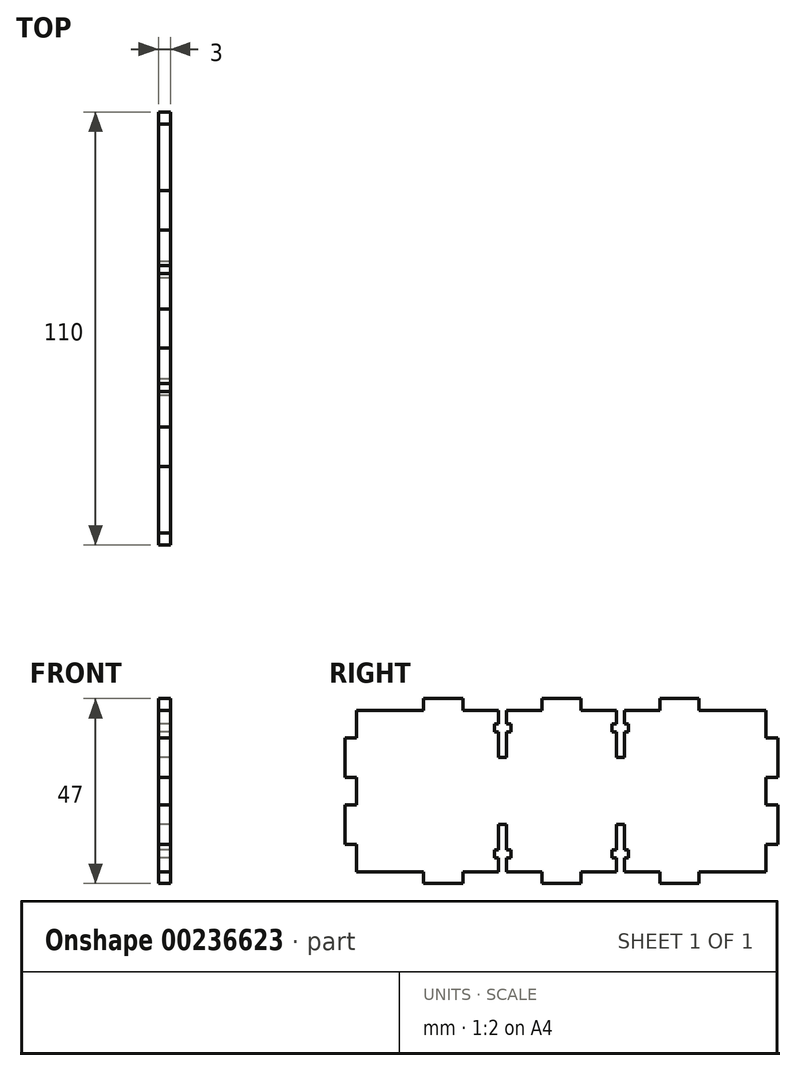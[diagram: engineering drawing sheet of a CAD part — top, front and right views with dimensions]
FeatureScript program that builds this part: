
annotation { "Feature Type Name" : "Feature", "Feature Type Description" : "" }
export const myFeature = defineFeature(function(context is Context, id is Id, definition is map)
    precondition{}
    {
        {
            var Q0;
            Q0=qCreatedBy(makeId("Right.planeOp"),FACE);
            var sketch = newSketch(context, id + "F0", { "sketchPlane" : qUnion([Q0])});
            skLineSegment(sketch, "E0", {"start": v(-52.38, -20.38) * mm, "end": v(-52.38, -13.38) * mm});
            skLineSegment(sketch, "E1", {"start": v(-52.38, -13.38) * mm, "end": v(-55.38, -13.38) * mm});
            skLineSegment(sketch, "E2", {"start": v(-55.38, -13.38) * mm, "end": v(-55.38, -3.38) * mm});
            skLineSegment(sketch, "E3", {"start": v(-55.38, -3.38) * mm, "end": v(-52.38, -3.38) * mm});
            skLineSegment(sketch, "E4", {"start": v(-52.38, -3.38) * mm, "end": v(-52.38, 0.12) * mm});
            skLineSegment(sketch, "E5", {"start": v(-52.38, -20.38) * mm, "end": v(-35.38, -20.38) * mm});
            skLineSegment(sketch, "E6", {"start": v(-35.38, -20.38) * mm, "end": v(-35.38, -23.38) * mm});
            skLineSegment(sketch, "E7", {"start": v(-35.38, -23.38) * mm, "end": v(-25.38, -23.38) * mm});
            skLineSegment(sketch, "E8", {"start": v(-25.38, -20.38) * mm, "end": v(-25.38, -23.38) * mm});
            skLineSegment(sketch, "E9", {"start": v(-25.38, -20.38) * mm, "end": v(-16.38, -20.38) * mm});
            skLineSegment(sketch, "E10", {"start": v(-16.38, -20.38) * mm, "end": v(-16.38, -16.88) * mm});
            skLineSegment(sketch, "E11", {"start": v(-16.38, -16.88) * mm, "end": v(-17.38, -16.88) * mm});
            skLineSegment(sketch, "E12", {"start": v(-17.38, -16.88) * mm, "end": v(-17.38, -14.88) * mm});
            skLineSegment(sketch, "E13", {"start": v(-17.38, -14.88) * mm, "end": v(-16.38, -14.88) * mm});
            skLineSegment(sketch, "E14", {"start": v(-16.38, -14.88) * mm, "end": v(-16.38, -8.38) * mm});
            skLineSegment(sketch, "E15", {"start": v(-16.38, -8.38) * mm, "end": v(-14.38, -8.38) * mm});
            skLineSegment(sketch, "E16", {"start": v(-14.38, -8.38) * mm, "end": v(-14.38, -14.88) * mm});
            skLineSegment(sketch, "E17", {"start": v(-14.38, -14.88) * mm, "end": v(-13.24, -14.88) * mm});
            skLineSegment(sketch, "E18", {"start": v(-14.38, -16.88) * mm, "end": v(-13.24, -16.88) * mm});
            skLineSegment(sketch, "E19", {"start": v(-14.38, -20.38) * mm, "end": v(-14.38, -16.88) * mm});
            skLineSegment(sketch, "E20", {"start": v(-14.38, -20.38) * mm, "end": v(-5.38, -20.38) * mm});
            skLineSegment(sketch, "E21", {"start": v(-13.24, -16.88) * mm, "end": v(-13.24, -14.88) * mm});
            skLineSegment(sketch, "E22", {"start": v(-5.38, -20.38) * mm, "end": v(-5.38, -23.38) * mm});
            skLineSegment(sketch, "E23", {"start": v(-5.38, -23.38) * mm, "end": v(-0.38, -23.38) * mm});
            skLineSegment(sketch, "E24", {"start": v(-52.38, 0.12) * mm, "end": v(-0.38, 0.12) * mm, "construction": true});
            skLineSegment(sketch, "E25", {"start": v(-0.38, 0.12) * mm, "end": v(-0.38, -23.38) * mm, "construction": true});
            skLineSegment(sketch, "E26.MirrorCS", {"start": v(-17.38, 15.12) * mm, "end": v(-16.38, 15.12) * mm});
            skLineSegment(sketch, "E27.MirrorCS", {"start": v(-13.24, 17.12) * mm, "end": v(-13.24, 15.12) * mm});
            skLineSegment(sketch, "E28.MirrorCS", {"start": v(-16.38, 17.12) * mm, "end": v(-17.38, 17.12) * mm});
            skLineSegment(sketch, "E29.MirrorCS", {"start": v(-17.38, 17.12) * mm, "end": v(-17.38, 15.12) * mm});
            skLineSegment(sketch, "E30.MirrorCS", {"start": v(-14.38, 15.12) * mm, "end": v(-13.24, 15.12) * mm});
            skLineSegment(sketch, "E31.MirrorCS", {"start": v(-14.38, 17.12) * mm, "end": v(-13.24, 17.12) * mm});
            skLineSegment(sketch, "E32.MirrorCS", {"start": v(-16.38, 8.62) * mm, "end": v(-14.38, 8.62) * mm});
            skLineSegment(sketch, "E33.MirrorCS", {"start": v(-16.38, 20.62) * mm, "end": v(-16.38, 17.12) * mm});
            skLineSegment(sketch, "E34.MirrorCS", {"start": v(-25.38, 20.62) * mm, "end": v(-25.38, 23.62) * mm});
            skLineSegment(sketch, "E35.MirrorCS", {"start": v(-52.38, 13.62) * mm, "end": v(-55.38, 13.62) * mm});
            skLineSegment(sketch, "E36.MirrorCS", {"start": v(-16.38, 15.12) * mm, "end": v(-16.38, 8.62) * mm});
            skLineSegment(sketch, "E37.MirrorCS", {"start": v(-14.38, 20.62) * mm, "end": v(-14.38, 17.12) * mm});
            skLineSegment(sketch, "E38.MirrorCS", {"start": v(-25.38, 20.62) * mm, "end": v(-16.38, 20.62) * mm});
            skLineSegment(sketch, "E39.MirrorCS", {"start": v(-14.38, 8.62) * mm, "end": v(-14.38, 15.12) * mm});
            skLineSegment(sketch, "E40.MirrorCS", {"start": v(-14.38, 20.62) * mm, "end": v(-5.38, 20.62) * mm});
            skLineSegment(sketch, "E41.MirrorCS", {"start": v(-52.38, 20.62) * mm, "end": v(-35.38, 20.62) * mm});
            skLineSegment(sketch, "E42.MirrorCS", {"start": v(-35.38, 20.62) * mm, "end": v(-35.38, 23.62) * mm});
            skLineSegment(sketch, "E43.MirrorCS", {"start": v(-55.38, 13.62) * mm, "end": v(-55.38, 3.62) * mm});
            skLineSegment(sketch, "E44.MirrorCS", {"start": v(-55.38, 3.62) * mm, "end": v(-52.38, 3.62) * mm});
            skLineSegment(sketch, "E45.MirrorCS", {"start": v(-52.38, 20.62) * mm, "end": v(-52.38, 13.62) * mm});
            skLineSegment(sketch, "E46.MirrorCS", {"start": v(-5.38, 20.62) * mm, "end": v(-5.38, 23.62) * mm});
            skLineSegment(sketch, "E47.MirrorCS", {"start": v(-35.38, 23.62) * mm, "end": v(-25.38, 23.62) * mm});
            skLineSegment(sketch, "E48.MirrorCS", {"start": v(-52.38, 3.62) * mm, "end": v(-52.38, 0.12) * mm});
            skLineSegment(sketch, "E49.MirrorCS", {"start": v(-5.38, 23.62) * mm, "end": v(-0.38, 23.62) * mm});
            skLineSegment(sketch, "E50.MirrorCS", {"start": v(-0.38, 0.12) * mm, "end": v(-0.38, 23.62) * mm, "construction": true});
            skLineSegment(sketch, "E51.MirrorCS", {"start": v(16.62, 17.12) * mm, "end": v(16.62, 15.12) * mm});
            skLineSegment(sketch, "E52.MirrorCS", {"start": v(16.62, 15.12) * mm, "end": v(15.62, 15.12) * mm});
            skLineSegment(sketch, "E53.MirrorCS", {"start": v(15.62, 8.62) * mm, "end": v(13.62, 8.62) * mm});
            skLineSegment(sketch, "E54.MirrorCS", {"start": v(13.62, 17.12) * mm, "end": v(12.48, 17.12) * mm});
            skLineSegment(sketch, "E55.MirrorCS", {"start": v(13.62, -16.88) * mm, "end": v(12.48, -16.88) * mm});
            skLineSegment(sketch, "E56.MirrorCS", {"start": v(15.62, -16.88) * mm, "end": v(16.62, -16.88) * mm});
            skLineSegment(sketch, "E57.MirrorCS", {"start": v(16.62, -16.88) * mm, "end": v(16.62, -14.88) * mm});
            skLineSegment(sketch, "E58.MirrorCS", {"start": v(13.62, -14.88) * mm, "end": v(12.48, -14.88) * mm});
            skLineSegment(sketch, "E59.MirrorCS", {"start": v(12.48, 17.12) * mm, "end": v(12.48, 15.12) * mm});
            skLineSegment(sketch, "E60.MirrorCS", {"start": v(13.62, 15.12) * mm, "end": v(12.48, 15.12) * mm});
            skLineSegment(sketch, "E61.MirrorCS", {"start": v(16.62, -14.88) * mm, "end": v(15.62, -14.88) * mm});
            skLineSegment(sketch, "E62.MirrorCS", {"start": v(12.48, -16.88) * mm, "end": v(12.48, -14.88) * mm});
            skLineSegment(sketch, "E63.MirrorCS", {"start": v(15.62, 17.12) * mm, "end": v(16.62, 17.12) * mm});
            skLineSegment(sketch, "E64.MirrorCS", {"start": v(15.62, -8.38) * mm, "end": v(13.62, -8.38) * mm});
            skLineSegment(sketch, "E65.MirrorCS", {"start": v(24.62, 20.62) * mm, "end": v(24.62, 23.62) * mm});
            skLineSegment(sketch, "E66.MirrorCS", {"start": v(13.62, -20.38) * mm, "end": v(4.62, -20.38) * mm});
            skLineSegment(sketch, "E67.MirrorCS", {"start": v(51.62, 20.62) * mm, "end": v(51.62, 13.62) * mm});
            skLineSegment(sketch, "E68.MirrorCS", {"start": v(34.62, 20.62) * mm, "end": v(34.62, 23.62) * mm});
            skLineSegment(sketch, "E69.MirrorCS", {"start": v(13.62, -20.38) * mm, "end": v(13.62, -16.88) * mm});
            skLineSegment(sketch, "E70.MirrorCS", {"start": v(13.62, -8.38) * mm, "end": v(13.62, -14.88) * mm});
            skLineSegment(sketch, "E71.MirrorCS", {"start": v(15.62, 15.12) * mm, "end": v(15.62, 8.62) * mm});
            skLineSegment(sketch, "E72.MirrorCS", {"start": v(51.62, 3.62) * mm, "end": v(51.62, 0.12) * mm});
            skLineSegment(sketch, "E73.MirrorCS", {"start": v(51.62, 13.62) * mm, "end": v(54.62, 13.62) * mm});
            skLineSegment(sketch, "E74.MirrorCS", {"start": v(34.62, 23.62) * mm, "end": v(24.62, 23.62) * mm});
            skLineSegment(sketch, "E75.MirrorCS", {"start": v(15.62, -20.38) * mm, "end": v(15.62, -16.88) * mm});
            skLineSegment(sketch, "E76.MirrorCS", {"start": v(15.62, 20.62) * mm, "end": v(15.62, 17.12) * mm});
            skLineSegment(sketch, "E77.MirrorCS", {"start": v(34.62, -20.38) * mm, "end": v(34.62, -23.38) * mm});
            skLineSegment(sketch, "E78.MirrorCS", {"start": v(51.62, -20.38) * mm, "end": v(51.62, -13.38) * mm});
            skLineSegment(sketch, "E79.MirrorCS", {"start": v(4.62, 23.62) * mm, "end": v(-0.38, 23.62) * mm});
            skLineSegment(sketch, "E80.MirrorCS", {"start": v(24.62, -20.38) * mm, "end": v(15.62, -20.38) * mm});
            skLineSegment(sketch, "E81.MirrorCS", {"start": v(4.62, -20.38) * mm, "end": v(4.62, -23.38) * mm});
            skLineSegment(sketch, "E82.MirrorCS", {"start": v(51.62, -13.38) * mm, "end": v(54.62, -13.38) * mm});
            skLineSegment(sketch, "E83.MirrorCS", {"start": v(24.62, 20.62) * mm, "end": v(15.62, 20.62) * mm});
            skLineSegment(sketch, "E84.MirrorCS", {"start": v(54.62, 13.62) * mm, "end": v(54.62, 3.62) * mm});
            skLineSegment(sketch, "E85.MirrorCS", {"start": v(54.62, -13.38) * mm, "end": v(54.62, -3.38) * mm});
            skLineSegment(sketch, "E86.MirrorCS", {"start": v(13.62, 8.62) * mm, "end": v(13.62, 15.12) * mm});
            skLineSegment(sketch, "E87.MirrorCS", {"start": v(4.62, -23.38) * mm, "end": v(-0.38, -23.38) * mm});
            skLineSegment(sketch, "E88.MirrorCS", {"start": v(13.62, 20.62) * mm, "end": v(13.62, 17.12) * mm});
            skLineSegment(sketch, "E89.MirrorCS", {"start": v(4.62, 20.62) * mm, "end": v(4.62, 23.62) * mm});
            skLineSegment(sketch, "E90.MirrorCS", {"start": v(13.62, 20.62) * mm, "end": v(4.62, 20.62) * mm});
            skLineSegment(sketch, "E91.MirrorCS", {"start": v(51.62, 0.12) * mm, "end": v(-0.38, 0.12) * mm, "construction": true});
            skLineSegment(sketch, "E92.MirrorCS", {"start": v(54.62, 3.62) * mm, "end": v(51.62, 3.62) * mm});
            skLineSegment(sketch, "E93.MirrorCS", {"start": v(51.62, -20.38) * mm, "end": v(34.62, -20.38) * mm});
            skLineSegment(sketch, "E94.MirrorCS", {"start": v(34.62, -23.38) * mm, "end": v(24.62, -23.38) * mm});
            skLineSegment(sketch, "E95.MirrorCS", {"start": v(15.62, -14.88) * mm, "end": v(15.62, -8.38) * mm});
            skLineSegment(sketch, "E96.MirrorCS", {"start": v(24.62, -20.38) * mm, "end": v(24.62, -23.38) * mm});
            skLineSegment(sketch, "E97.MirrorCS", {"start": v(51.62, 20.62) * mm, "end": v(34.62, 20.62) * mm});
            skLineSegment(sketch, "E98.MirrorCS", {"start": v(51.62, -3.38) * mm, "end": v(51.62, 0.12) * mm});
            skLineSegment(sketch, "E99.MirrorCS", {"start": v(54.62, -3.38) * mm, "end": v(51.62, -3.38) * mm});
            skSolve(sketch);
        }
        {
            var Q0;
            Q0=qSketchRegion(id+"F0",true);
            extrude(context, id + "F1", {"entities" : qUnion([Q0]), "depth" : 3 * mm});
        }
    });
